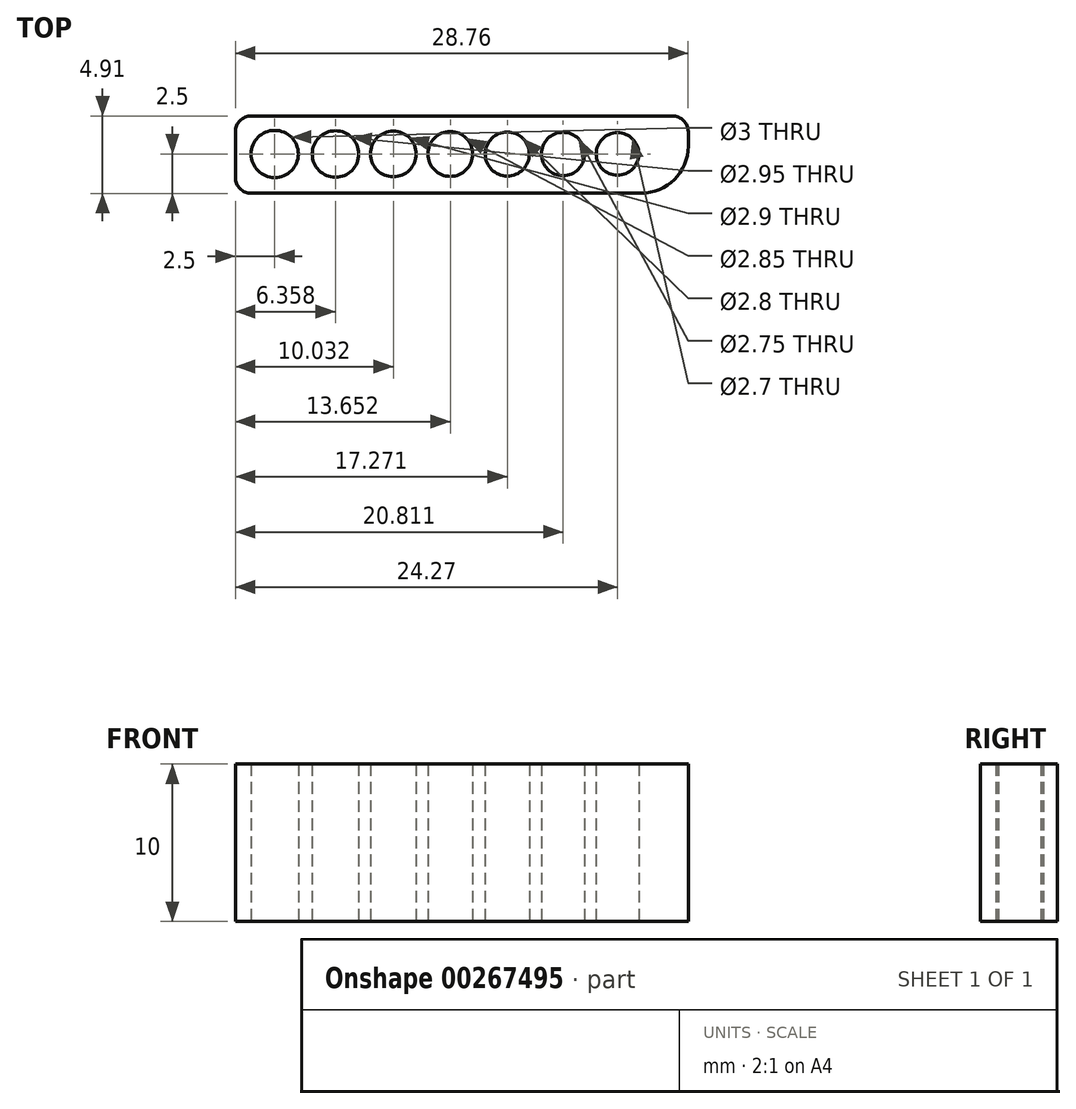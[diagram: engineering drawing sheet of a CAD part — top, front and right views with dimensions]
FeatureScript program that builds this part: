
annotation { "Feature Type Name" : "Feature", "Feature Type Description" : "" }
export const myFeature = defineFeature(function(context is Context, id is Id, definition is map)
    precondition{}
    {
        {
            var Q0;
            Q0=qCreatedBy(makeId("Top.planeOp"),FACE);
            var sketch = newSketch(context, id + "F0", { "sketchPlane" : qUnion([Q0])});
            skCircle(sketch, "E0", {"center": v(0, 0) * mm, "radius": 1.5 * mm});
            skCircle(sketch, "E1", {"center": v(3.86, 0) * mm, "radius": 1.48 * mm});
            skCircle(sketch, "E2", {"center": v(7.53, 0) * mm, "radius": 1.45 * mm});
            skCircle(sketch, "E3", {"center": v(11.15, 0) * mm, "radius": 1.43 * mm});
            skCircle(sketch, "E4", {"center": v(14.77, 0) * mm, "radius": 1.4 * mm});
            skCircle(sketch, "E5", {"center": v(18.31, 0) * mm, "radius": 1.38 * mm});
            skCircle(sketch, "E6", {"center": v(21.77, 0) * mm, "radius": 1.35 * mm});
            skLineSegment(sketch, "E7.bottom", {"start": v(-1.5, 2.41) * mm, "end": v(25.26, 2.41) * mm});
            skLineSegment(sketch, "E7.top", {"start": v(-1.5, -2.5) * mm, "end": v(23.26, -2.5) * mm});
            skLineSegment(sketch, "E7.left", {"start": v(-2.5, 1.41) * mm, "end": v(-2.5, -1.5) * mm});
            skLineSegment(sketch, "E7.right", {"start": v(26.26, 1.41) * mm, "end": v(26.26, 0.5) * mm});
            skPoint(sketch, "E8.visualSharp", {"position": v(26.26, 2.41) * mm});
            skArc(sketch, "E8.filletArc", {"start": v(26.26, 1.41) * mm, "mid": v(25.97, 2.12) * mm, "end": v(25.26, 2.41) * mm});
            skPoint(sketch, "E9.visualSharp", {"position": v(-2.5, 2.41) * mm});
            skArc(sketch, "E9.filletArc", {"start": v(-1.5, 2.41) * mm, "mid": v(-2.2, 2.12) * mm, "end": v(-2.5, 1.41) * mm});
            skPoint(sketch, "E10.visualSharp", {"position": v(-2.5, -2.5) * mm});
            skArc(sketch, "E10.filletArc", {"start": v(-2.5, -1.5) * mm, "mid": v(-2.2, -2.2) * mm, "end": v(-1.5, -2.5) * mm});
            skLineSegment(sketch, "E11", {"start": v(23.26, -2.5) * mm, "end": v(23.26, -2.5) * mm});
            skLineSegment(sketch, "E12", {"start": v(26.26, 0.5) * mm, "end": v(26.26, 0.5) * mm});
            skPoint(sketch, "E13.visualSharp", {"position": v(26.26, -2.5) * mm});
            skArc(sketch, "E13.filletArc", {"start": v(23.26, -2.5) * mm, "mid": v(25.39, -1.62) * mm, "end": v(26.26, 0.5) * mm});
            skSolve(sketch);
        }
        {
            var Q0;
            Q0 = qSketchRegion(id + "F0", true);
            extrude(context, id + "F1", {"entities" : qUnion([Q0]), "depth" : 10 * mm});
        }
    });
